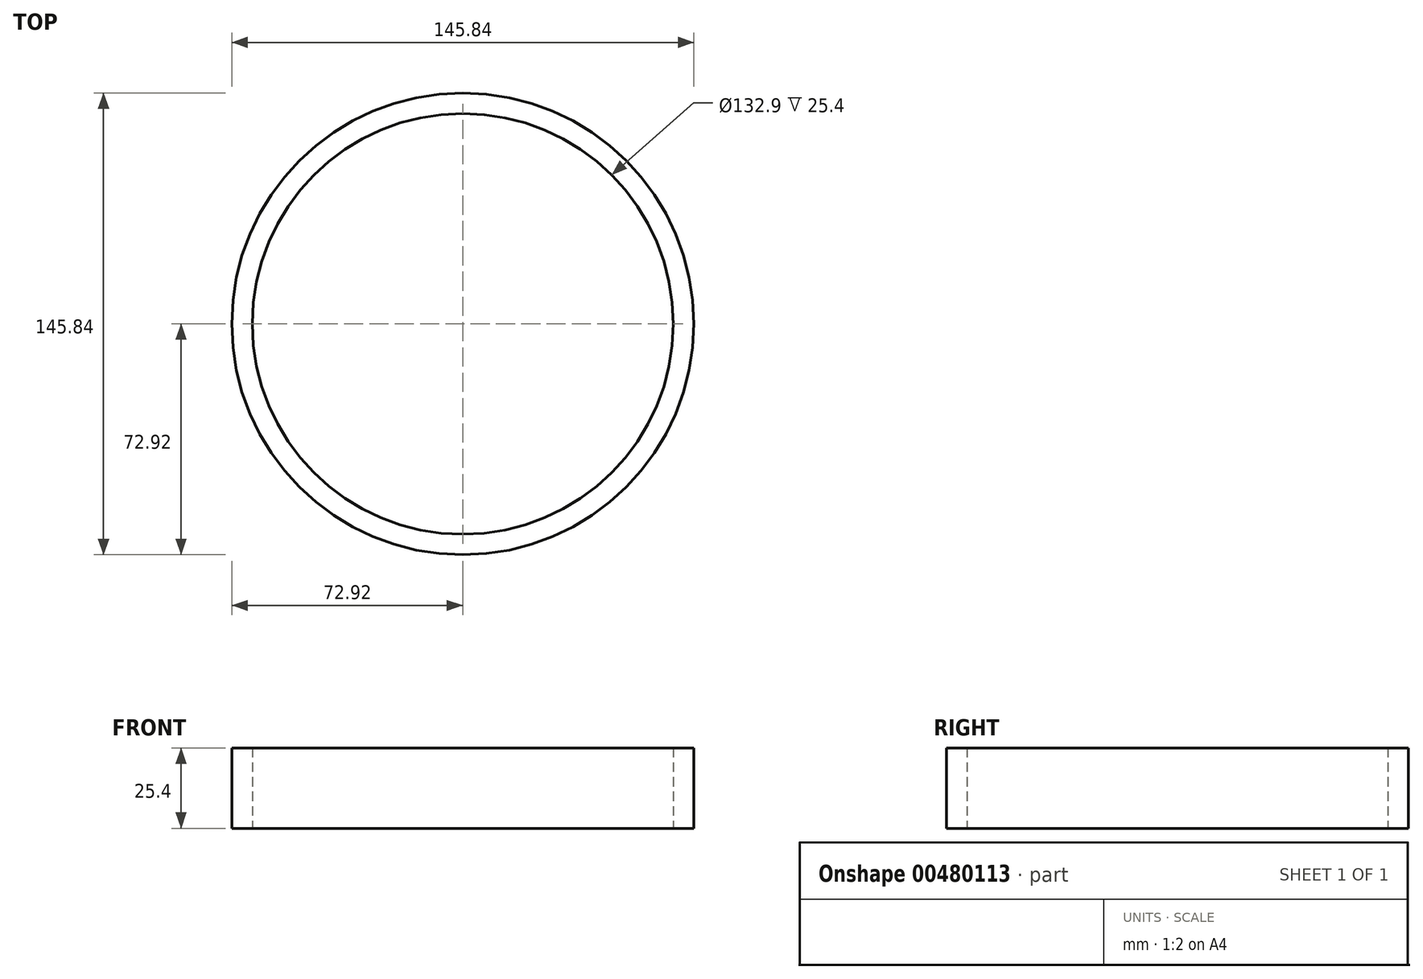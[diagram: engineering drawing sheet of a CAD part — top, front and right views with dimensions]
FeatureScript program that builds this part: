
annotation { "Feature Type Name" : "Feature", "Feature Type Description" : "" }
export const myFeature = defineFeature(function(context is Context, id is Id, definition is map)
    precondition{}
    {
        {
            var Q0;
            Q0=qCreatedBy(makeId("Top.planeOp"),FACE);
            var sketch = newSketch(context, id + "F0", { "sketchPlane" : qUnion([Q0])});
            skCircle(sketch, "E0", {"center": v(0, 0) * mm, "radius": 72.92 * mm});
            skCircle(sketch, "E1", {"center": v(0, 0) * mm, "radius": 66.45 * mm});
            skSolve(sketch);
        }
        {
            var Q0;
            Q0 = qSketchRegion(id + "F0", true);
            extrude(context, id + "F1", {"entities" : qUnion([Q0]), "depth" : 25.4 * mm});
        }
    });
